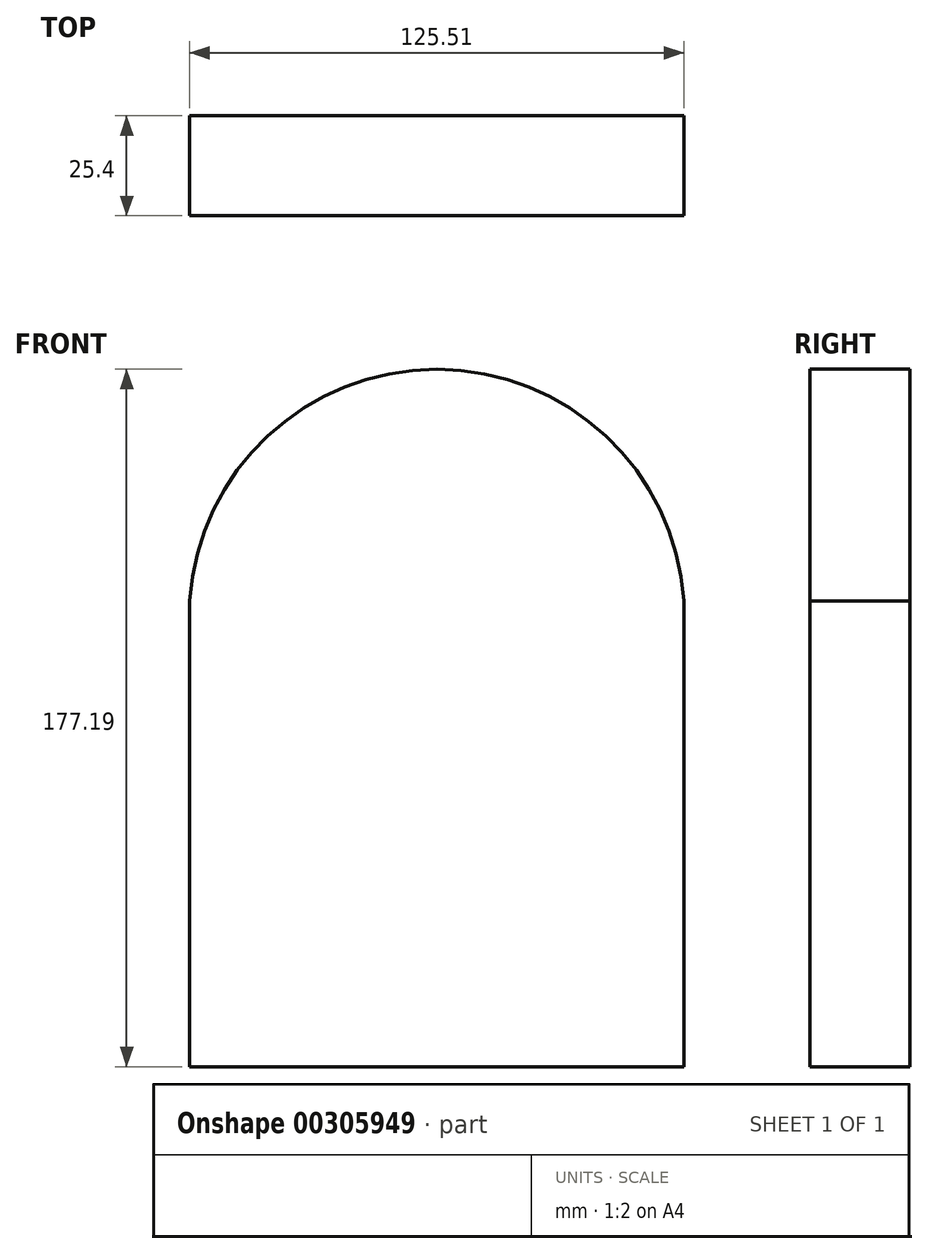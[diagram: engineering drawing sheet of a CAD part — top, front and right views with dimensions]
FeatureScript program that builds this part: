
annotation { "Feature Type Name" : "Feature", "Feature Type Description" : "" }
export const myFeature = defineFeature(function(context is Context, id is Id, definition is map)
    precondition{}
    {
        {
            var Q0;
            Q0=qCreatedBy(makeId("Front.planeOp"),FACE);
            var sketch = newSketch(context, id + "F0", { "sketchPlane" : qUnion([Q0])});
            skLineSegment(sketch, "E0", {"start": v(-97.82, 40.44) * mm, "end": v(-97.82, -77.94) * mm});
            skLineSegment(sketch, "E1", {"start": v(-97.82, -77.94) * mm, "end": v(27.69, -77.94) * mm});
            skLineSegment(sketch, "E2", {"start": v(27.69, -77.94) * mm, "end": v(27.69, 40.44) * mm});
            skArc(sketch, "E3", {"start": v(27.69, 40.44) * mm, "mid": v(-35.06, 99.25) * mm, "end": v(-97.82, 40.44) * mm});
            skSolve(sketch);
        }
        {
            var Q0;
            Q0=makeQuery(id+"F0.imprint","IMPRINT",FACE,{"disambiguationData":[TD([[makeQuery(id+"F0.imprint","IMPRINT",EDGE,{"derivedFrom":sQuery(id+"F0.wireOp",EDGE,"E0")}),1.0]])]});
            extrude(context, id + "F1", {"entities" : qUnion([Q0]), "depth" : 25.4 * mm});
        }
    });
